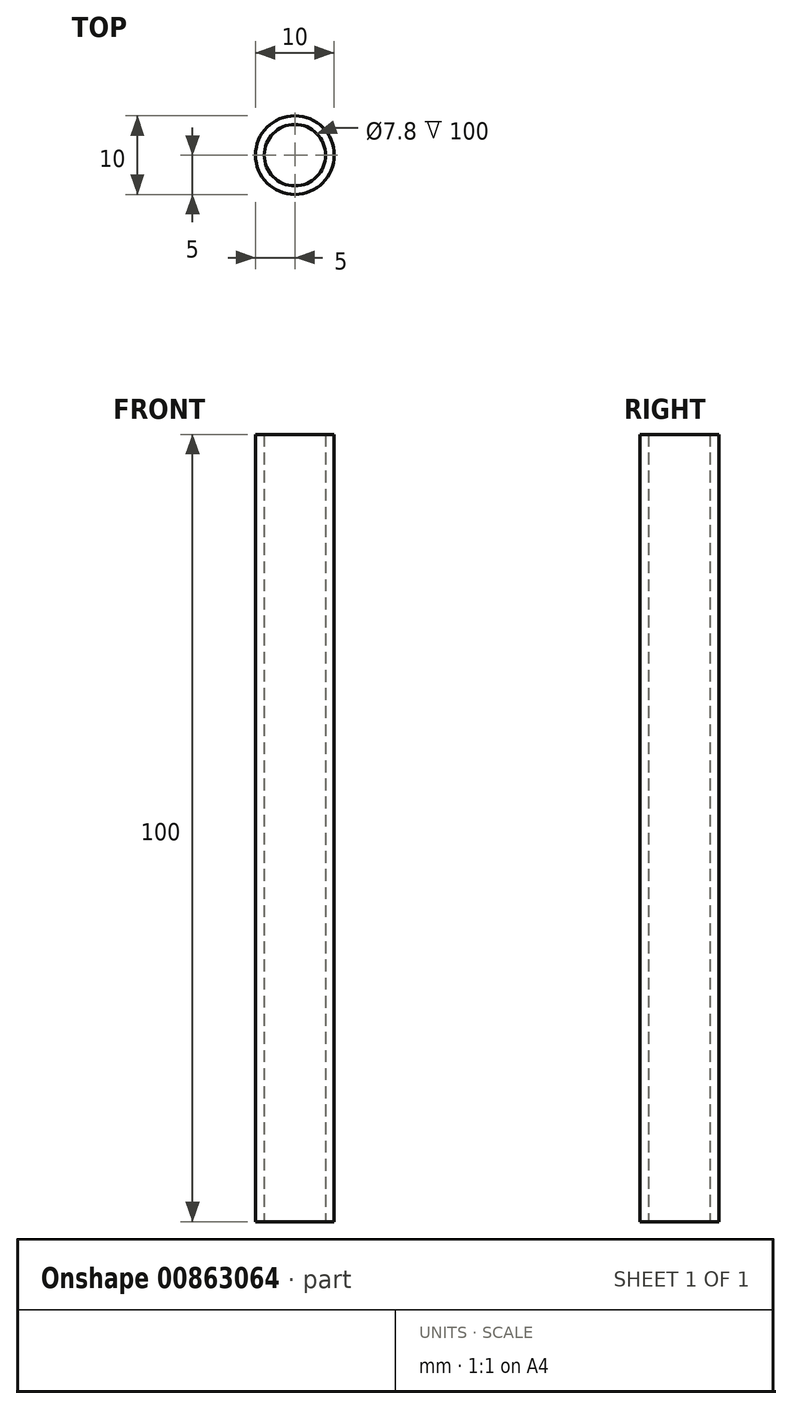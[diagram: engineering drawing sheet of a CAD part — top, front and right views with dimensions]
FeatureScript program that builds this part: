
annotation { "Feature Type Name" : "Feature", "Feature Type Description" : "" }
export const myFeature = defineFeature(function(context is Context, id is Id, definition is map)
    precondition{}
    {
        {
            var Q0;
            Q0=qCreatedBy(makeId("Top.planeOp"),FACE);
            var sketch = newSketch(context, id + "F0", { "sketchPlane" : qUnion([Q0])});
            skCircle(sketch, "E0", {"center": v(0, 0) * mm, "radius": 3.9 * mm});
            skCircle(sketch, "E1", {"center": v(0, 0) * mm, "radius": 5 * mm});
            skSolve(sketch);
        }
        {
            var Q0;
            Q0=makeQuery(id+"F0.imprint","IMPRINT",FACE,{"disambiguationData":[TD([[makeQuery(id+"F0.imprint","IMPRINT",EDGE,{"derivedFrom":sQuery(id+"F0.wireOp",EDGE,"E0")}),-1.0]])]});
            extrude(context, id + "F1", {"entities" : qUnion([Q0]), "depth" : 100 * mm, "offsetDistance" : 25 * mm});
        }
    });
